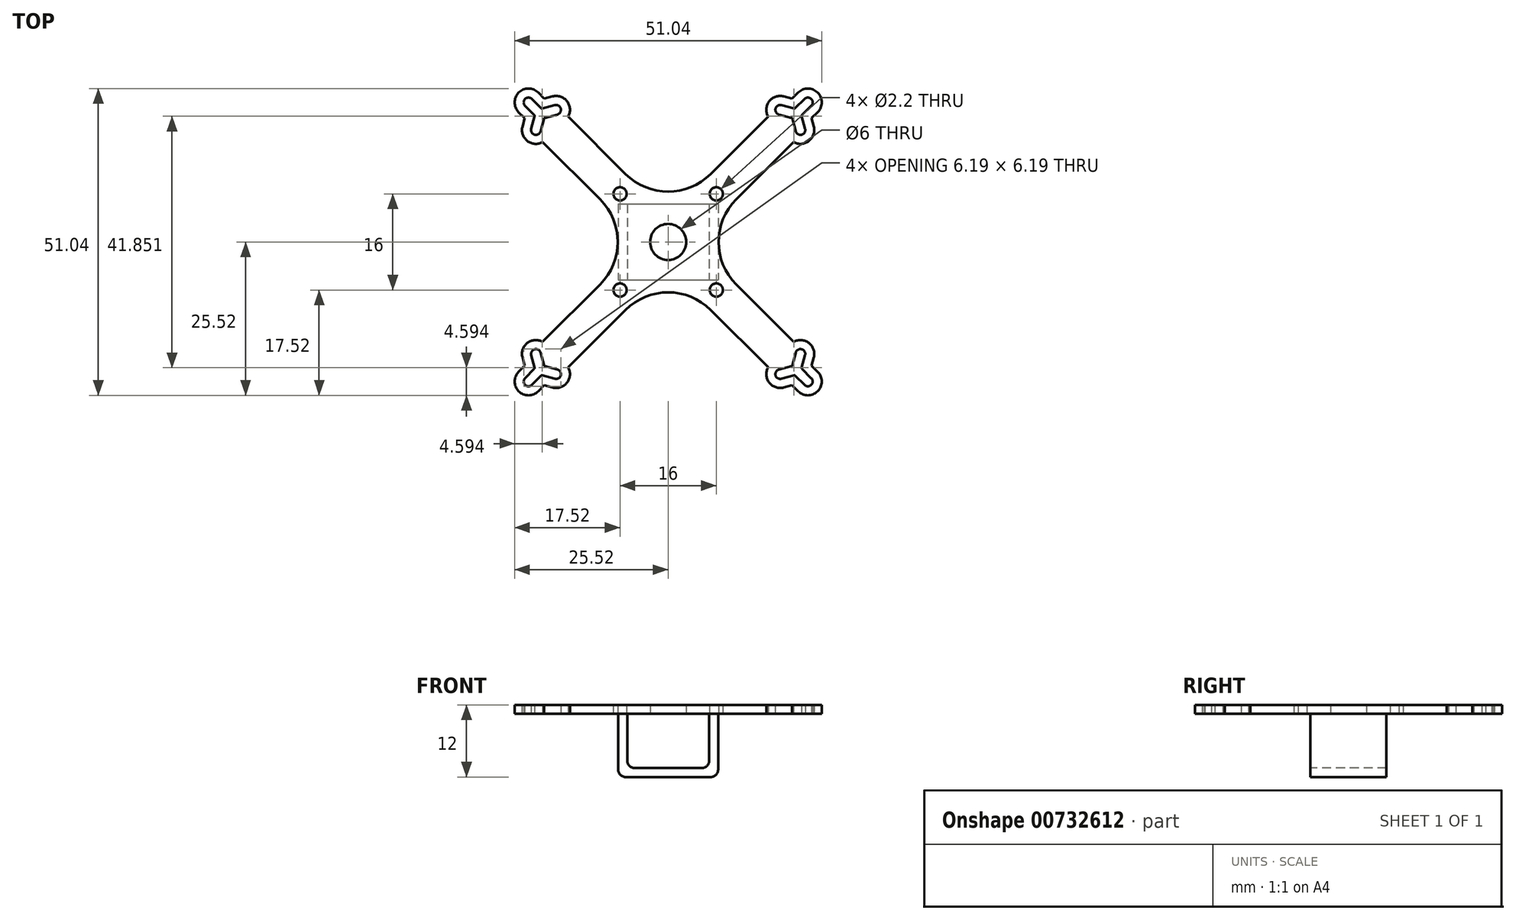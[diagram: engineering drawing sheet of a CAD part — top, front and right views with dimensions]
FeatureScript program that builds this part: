
annotation { "Feature Type Name" : "Feature", "Feature Type Description" : "" }
export const myFeature = defineFeature(function(context is Context, id is Id, definition is map)
    precondition{}
    {
        {
            var Q0;
            Q0=qCreatedBy(makeId("Top.planeOp"),FACE);
            var sketch = newSketch(context, id + "F0", { "sketchPlane" : qUnion([Q0])});
            skLineSegment(sketch, "E0", {"start": v(-7, 6.31) * mm, "end": v(7, 6.31) * mm});
            skLineSegment(sketch, "E1", {"start": v(-7, -6.31) * mm, "end": v(7, -6.31) * mm});
            skPoint(sketch, "E2.middle", {"position": v(0, 0) * mm});
            skLineSegment(sketch, "E3", {"start": v(-10, 10) * mm, "end": v(-8, 8) * mm, "construction": true});
            skPoint(sketch, "E4.center", {"position": v(-21.28, -21.28) * mm});
            skLineSegment(sketch, "E5.0", {"start": v(-20.94, -22.2) * mm, "end": v(-18.83, -22.76) * mm});
            skLineSegment(sketch, "E6.0", {"start": v(-20.53, -20.65) * mm, "end": v(-18.41, -21.22) * mm});
            skLineSegment(sketch, "E7.1.0", {"start": v(-22.24, -21.11) * mm, "end": v(-23.79, -22.66) * mm});
            skLineSegment(sketch, "E7.1.1", {"start": v(-21.11, -22.24) * mm, "end": v(-22.66, -23.79) * mm});
            skLineSegment(sketch, "E7.2.0", {"start": v(-20.65, -20.53) * mm, "end": v(-21.22, -18.41) * mm});
            skLineSegment(sketch, "E7.2.1", {"start": v(-22.2, -20.94) * mm, "end": v(-22.76, -18.83) * mm});
            skPoint(sketch, "E8.visualSharp", {"position": v(-22.17, -21.04) * mm});
            skArc(sketch, "E8.filletArc", {"start": v(-22.24, -21.11) * mm, "mid": v(-22.2, -21.03) * mm, "end": v(-22.2, -20.94) * mm});
            skPoint(sketch, "E9.visualSharp", {"position": v(-20.62, -20.62) * mm});
            skArc(sketch, "E9.filletArc", {"start": v(-20.65, -20.53) * mm, "mid": v(-20.6, -20.6) * mm, "end": v(-20.53, -20.65) * mm});
            skPoint(sketch, "E10.visualSharp", {"position": v(-21.04, -22.17) * mm});
            skArc(sketch, "E10.filletArc", {"start": v(-20.94, -22.2) * mm, "mid": v(-21.03, -22.2) * mm, "end": v(-21.11, -22.24) * mm});
            skLineSegment(sketch, "E11.0", {"start": v(-23.84, -20.6) * mm, "end": v(-24.21, -19.22) * mm});
            skLineSegment(sketch, "E12.0", {"start": v(-23.84, -20.6) * mm, "end": v(-24.85, -21.6) * mm});
            skArc(sketch, "E13.0", {"start": v(-19.53, -24.1) * mm, "mid": v(-16.91, -23.53) * mm, "end": v(-16.62, -20.86) * mm});
            skLineSegment(sketch, "E14.0", {"start": v(-20.6, -23.84) * mm, "end": v(-19.22, -24.21) * mm});
            skLineSegment(sketch, "E15.0", {"start": v(-20.6, -23.84) * mm, "end": v(-21.6, -24.85) * mm});
            skArc(sketch, "E16.0", {"start": v(-24.85, -21.6) * mm, "mid": v(-24.85, -24.85) * mm, "end": v(-21.6, -24.85) * mm});
            skArc(sketch, "E17", {"start": v(-23.79, -22.66) * mm, "mid": v(-23.79, -23.79) * mm, "end": v(-22.66, -23.79) * mm});
            skArc(sketch, "E18.1.0", {"start": v(-18.83, -22.76) * mm, "mid": v(-17.85, -22.2) * mm, "end": v(-18.41, -21.22) * mm});
            skArc(sketch, "E18.2.0", {"start": v(-21.22, -18.41) * mm, "mid": v(-22.2, -17.85) * mm, "end": v(-22.76, -18.83) * mm});
            skArc(sketch, "E19.trimOffspring", {"start": v(-20.86, -16.62) * mm, "mid": v(-23.53, -16.91) * mm, "end": v(-24.1, -19.53) * mm});
            skLineSegment(sketch, "E20.1.2", {"start": v(20.94, -22.2) * mm, "end": v(18.83, -22.76) * mm});
            skArc(sketch, "E20.1.3", {"start": v(16.62, -20.86) * mm, "mid": v(16.91, -23.53) * mm, "end": v(19.53, -24.1) * mm});
            skArc(sketch, "E20.1.4", {"start": v(18.41, -21.22) * mm, "mid": v(17.85, -22.2) * mm, "end": v(18.83, -22.76) * mm});
            skLineSegment(sketch, "E20.1.5", {"start": v(20.65, -20.53) * mm, "end": v(21.22, -18.41) * mm});
            skArc(sketch, "E20.1.6", {"start": v(21.6, -24.85) * mm, "mid": v(24.85, -24.85) * mm, "end": v(24.85, -21.6) * mm});
            skLineSegment(sketch, "E20.1.7", {"start": v(22.2, -20.94) * mm, "end": v(22.76, -18.83) * mm});
            skArc(sketch, "E20.1.8", {"start": v(22.76, -18.83) * mm, "mid": v(22.2, -17.85) * mm, "end": v(21.22, -18.41) * mm});
            skPoint(sketch, "E20.1.9", {"position": v(22.17, -21.04) * mm});
            skLineSegment(sketch, "E20.1.10", {"start": v(20.53, -20.65) * mm, "end": v(18.41, -21.22) * mm});
            skLineSegment(sketch, "E20.1.11", {"start": v(23.84, -20.6) * mm, "end": v(24.85, -21.6) * mm});
            skPoint(sketch, "E20.1.12", {"position": v(21.28, -21.28) * mm});
            skLineSegment(sketch, "E20.1.13", {"start": v(22.24, -21.11) * mm, "end": v(23.79, -22.66) * mm});
            skLineSegment(sketch, "E20.1.14", {"start": v(23.84, -20.6) * mm, "end": v(24.21, -19.22) * mm});
            skLineSegment(sketch, "E20.1.15", {"start": v(20.6, -23.84) * mm, "end": v(21.6, -24.85) * mm});
            skLineSegment(sketch, "E20.1.16", {"start": v(21.11, -22.24) * mm, "end": v(22.66, -23.79) * mm});
            skArc(sketch, "E20.1.17", {"start": v(24.1, -19.53) * mm, "mid": v(23.53, -16.91) * mm, "end": v(20.86, -16.62) * mm});
            skLineSegment(sketch, "E20.1.18", {"start": v(20.6, -23.84) * mm, "end": v(19.22, -24.21) * mm});
            skArc(sketch, "E20.1.19", {"start": v(22.66, -23.79) * mm, "mid": v(23.79, -23.79) * mm, "end": v(23.79, -22.66) * mm});
            skPoint(sketch, "E20.1.20", {"position": v(20.62, -20.62) * mm});
            skPoint(sketch, "E20.1.21", {"position": v(21.04, -22.17) * mm});
            skPoint(sketch, "E20.1.22", {"position": v(21.28, -21.28) * mm});
            skPoint(sketch, "E20.1.23", {"position": v(21.28, -21.28) * mm});
            skArc(sketch, "E20.1.24", {"start": v(22.2, -20.94) * mm, "mid": v(22.2, -21.03) * mm, "end": v(22.24, -21.11) * mm});
            skArc(sketch, "E20.1.25", {"start": v(21.11, -22.24) * mm, "mid": v(21.03, -22.2) * mm, "end": v(20.94, -22.2) * mm});
            skArc(sketch, "E20.1.26", {"start": v(20.53, -20.65) * mm, "mid": v(20.6, -20.6) * mm, "end": v(20.65, -20.53) * mm});
            skLineSegment(sketch, "E20.2.2", {"start": v(22.2, 20.94) * mm, "end": v(22.76, 18.83) * mm});
            skArc(sketch, "E20.2.3", {"start": v(20.86, 16.62) * mm, "mid": v(23.53, 16.91) * mm, "end": v(24.1, 19.53) * mm});
            skArc(sketch, "E20.2.4", {"start": v(21.22, 18.41) * mm, "mid": v(22.2, 17.85) * mm, "end": v(22.76, 18.83) * mm});
            skLineSegment(sketch, "E20.2.5", {"start": v(20.53, 20.65) * mm, "end": v(18.41, 21.22) * mm});
            skArc(sketch, "E20.2.6", {"start": v(24.85, 21.6) * mm, "mid": v(24.85, 24.85) * mm, "end": v(21.6, 24.85) * mm});
            skLineSegment(sketch, "E20.2.7", {"start": v(20.94, 22.2) * mm, "end": v(18.83, 22.76) * mm});
            skArc(sketch, "E20.2.8", {"start": v(18.83, 22.76) * mm, "mid": v(17.85, 22.2) * mm, "end": v(18.41, 21.22) * mm});
            skPoint(sketch, "E20.2.9", {"position": v(21.04, 22.17) * mm});
            skLineSegment(sketch, "E20.2.10", {"start": v(20.65, 20.53) * mm, "end": v(21.22, 18.41) * mm});
            skLineSegment(sketch, "E20.2.11", {"start": v(20.6, 23.84) * mm, "end": v(21.6, 24.85) * mm});
            skPoint(sketch, "E20.2.12", {"position": v(21.28, 21.28) * mm});
            skLineSegment(sketch, "E20.2.13", {"start": v(21.11, 22.24) * mm, "end": v(22.66, 23.79) * mm});
            skLineSegment(sketch, "E20.2.14", {"start": v(20.6, 23.84) * mm, "end": v(19.22, 24.21) * mm});
            skLineSegment(sketch, "E20.2.15", {"start": v(23.84, 20.6) * mm, "end": v(24.85, 21.6) * mm});
            skLineSegment(sketch, "E20.2.16", {"start": v(22.24, 21.11) * mm, "end": v(23.79, 22.66) * mm});
            skArc(sketch, "E20.2.17", {"start": v(19.53, 24.1) * mm, "mid": v(16.91, 23.53) * mm, "end": v(16.62, 20.86) * mm});
            skLineSegment(sketch, "E20.2.18", {"start": v(23.84, 20.6) * mm, "end": v(24.21, 19.22) * mm});
            skArc(sketch, "E20.2.19", {"start": v(23.79, 22.66) * mm, "mid": v(23.79, 23.79) * mm, "end": v(22.66, 23.79) * mm});
            skPoint(sketch, "E20.2.20", {"position": v(20.62, 20.62) * mm});
            skPoint(sketch, "E20.2.21", {"position": v(22.17, 21.04) * mm});
            skPoint(sketch, "E20.2.22", {"position": v(21.28, 21.28) * mm});
            skPoint(sketch, "E20.2.23", {"position": v(21.28, 21.28) * mm});
            skArc(sketch, "E20.2.24", {"start": v(20.94, 22.2) * mm, "mid": v(21.03, 22.2) * mm, "end": v(21.11, 22.24) * mm});
            skArc(sketch, "E20.2.25", {"start": v(22.24, 21.11) * mm, "mid": v(22.2, 21.03) * mm, "end": v(22.2, 20.94) * mm});
            skArc(sketch, "E20.2.26", {"start": v(20.65, 20.53) * mm, "mid": v(20.6, 20.6) * mm, "end": v(20.53, 20.65) * mm});
            skLineSegment(sketch, "E20.3.2", {"start": v(-20.94, 22.2) * mm, "end": v(-18.83, 22.76) * mm});
            skArc(sketch, "E20.3.3", {"start": v(-16.62, 20.86) * mm, "mid": v(-16.91, 23.53) * mm, "end": v(-19.53, 24.1) * mm});
            skArc(sketch, "E20.3.4", {"start": v(-18.41, 21.22) * mm, "mid": v(-17.85, 22.2) * mm, "end": v(-18.83, 22.76) * mm});
            skLineSegment(sketch, "E20.3.5", {"start": v(-20.65, 20.53) * mm, "end": v(-21.22, 18.41) * mm});
            skArc(sketch, "E20.3.6", {"start": v(-21.6, 24.85) * mm, "mid": v(-24.85, 24.85) * mm, "end": v(-24.85, 21.6) * mm});
            skLineSegment(sketch, "E20.3.7", {"start": v(-22.2, 20.94) * mm, "end": v(-22.76, 18.83) * mm});
            skArc(sketch, "E20.3.8", {"start": v(-22.76, 18.83) * mm, "mid": v(-22.2, 17.85) * mm, "end": v(-21.22, 18.41) * mm});
            skPoint(sketch, "E20.3.9", {"position": v(-22.17, 21.04) * mm});
            skLineSegment(sketch, "E20.3.10", {"start": v(-20.53, 20.65) * mm, "end": v(-18.41, 21.22) * mm});
            skLineSegment(sketch, "E20.3.11", {"start": v(-23.84, 20.6) * mm, "end": v(-24.85, 21.6) * mm});
            skPoint(sketch, "E20.3.12", {"position": v(-21.28, 21.28) * mm});
            skLineSegment(sketch, "E20.3.13", {"start": v(-22.24, 21.11) * mm, "end": v(-23.79, 22.66) * mm});
            skLineSegment(sketch, "E20.3.14", {"start": v(-23.84, 20.6) * mm, "end": v(-24.21, 19.22) * mm});
            skLineSegment(sketch, "E20.3.15", {"start": v(-20.6, 23.84) * mm, "end": v(-21.6, 24.85) * mm});
            skLineSegment(sketch, "E20.3.16", {"start": v(-21.11, 22.24) * mm, "end": v(-22.66, 23.79) * mm});
            skArc(sketch, "E20.3.17", {"start": v(-24.1, 19.53) * mm, "mid": v(-23.53, 16.91) * mm, "end": v(-20.86, 16.62) * mm});
            skLineSegment(sketch, "E20.3.18", {"start": v(-20.6, 23.84) * mm, "end": v(-19.22, 24.21) * mm});
            skArc(sketch, "E20.3.19", {"start": v(-22.66, 23.79) * mm, "mid": v(-23.79, 23.79) * mm, "end": v(-23.79, 22.66) * mm});
            skPoint(sketch, "E20.3.20", {"position": v(-20.62, 20.62) * mm});
            skPoint(sketch, "E20.3.21", {"position": v(-21.04, 22.17) * mm});
            skPoint(sketch, "E20.3.22", {"position": v(-21.28, 21.28) * mm});
            skPoint(sketch, "E20.3.23", {"position": v(-21.28, 21.28) * mm});
            skArc(sketch, "E20.3.24", {"start": v(-22.2, 20.94) * mm, "mid": v(-22.2, 21.03) * mm, "end": v(-22.24, 21.11) * mm});
            skArc(sketch, "E20.3.25", {"start": v(-21.11, 22.24) * mm, "mid": v(-21.03, 22.2) * mm, "end": v(-20.94, 22.2) * mm});
            skArc(sketch, "E20.3.26", {"start": v(-20.53, 20.65) * mm, "mid": v(-20.6, 20.6) * mm, "end": v(-20.65, 20.53) * mm});
            skCircle(sketch, "E21", {"center": v(0, 0) * mm, "radius": 3 * mm});
            skLineSegment(sketch, "E22", {"start": v(-20.86, -16.62) * mm, "end": v(-11.31, -7.07) * mm});
            skLineSegment(sketch, "E23", {"start": v(-16.62, -20.86) * mm, "end": v(-7.07, -11.31) * mm});
            skLineSegment(sketch, "E24", {"start": v(-20.86, 16.62) * mm, "end": v(-11.31, 7.07) * mm});
            skLineSegment(sketch, "E25", {"start": v(-16.62, 20.86) * mm, "end": v(-7.07, 11.31) * mm});
            skLineSegment(sketch, "E26.trimOffspring", {"start": v(7.07, 11.31) * mm, "end": v(16.62, 20.86) * mm});
            skLineSegment(sketch, "E27.trimOffspring", {"start": v(11.31, -7.07) * mm, "end": v(20.86, -16.62) * mm});
            skLineSegment(sketch, "E28.trimOffspring", {"start": v(7.07, -11.31) * mm, "end": v(16.62, -20.86) * mm});
            skLineSegment(sketch, "E29.trimOffspring", {"start": v(11.31, 7.07) * mm, "end": v(20.86, 16.62) * mm});
            skPoint(sketch, "E30.visualSharp", {"position": v(-4.24, 0) * mm});
            skPoint(sketch, "E31.visualSharp", {"position": v(0, 4.24) * mm});
            skPoint(sketch, "E32.visualSharp", {"position": v(0, -4.24) * mm});
            skPoint(sketch, "E33.visualSharp", {"position": v(4.24, 0) * mm});
            skLineSegment(sketch, "E34", {"start": v(0, 6.31) * mm, "end": v(0, -6.31) * mm, "construction": true});
            skArc(sketch, "E35.filletArc", {"start": v(-11.31, -7.07) * mm, "mid": v(-8.38, 0) * mm, "end": v(-11.31, 7.07) * mm});
            skArc(sketch, "E36.filletArc", {"start": v(-7.07, 11.31) * mm, "mid": v(0, 8.38) * mm, "end": v(7.07, 11.31) * mm});
            skArc(sketch, "E37.filletArc", {"start": v(11.31, 7.07) * mm, "mid": v(8.38, 0) * mm, "end": v(11.31, -7.07) * mm});
            skArc(sketch, "E38.filletArc", {"start": v(7.07, -11.31) * mm, "mid": v(0, -8.38) * mm, "end": v(-7.07, -11.31) * mm});
            skLineSegment(sketch, "E39.0", {"start": v(-8.3, 6.31) * mm, "end": v(-8.3, -6.31) * mm});
            skLineSegment(sketch, "E40.0", {"start": v(8.3, 6.31) * mm, "end": v(8.3, -6.31) * mm});
            skLineSegment(sketch, "E41", {"start": v(-8.3, 6.31) * mm, "end": v(8.3, 6.31) * mm});
            skLineSegment(sketch, "E42", {"start": v(-8.3, -6.31) * mm, "end": v(8.3, -6.31) * mm});
            skPoint(sketch, "E43", {"position": v(-25.82, 23.88) * mm});
            skLineSegment(sketch, "E44", {"start": v(-25.26, 25.26) * mm, "end": v(-23.22, 23.22) * mm, "construction": true});
            skPoint(sketch, "E45.MirrorP", {"position": v(-23.88, 25.82) * mm});
            skLineSegment(sketch, "E46", {"start": v(-21.28, 21.28) * mm, "end": v(21.28, -21.28) * mm, "construction": true});
            skCircle(sketch, "E47", {"center": v(-8, 8) * mm, "radius": 1.1 * mm});
            skCircle(sketch, "E48.MirrorC", {"center": v(8, 8) * mm, "radius": 1.1 * mm});
            skCircle(sketch, "E49.MirrorC", {"center": v(-8, -8) * mm, "radius": 1.1 * mm});
            skCircle(sketch, "E50.MirrorC", {"center": v(8, -8) * mm, "radius": 1.1 * mm});
            skLineSegment(sketch, "E51", {"start": v(-25.51, 22.99) * mm, "end": v(-22.99, 25.51) * mm, "construction": true});
            skSolve(sketch);
        }
        {
            var Q0;
            Q0=makeQuery(id+"F0.imprint","IMPRINT",FACE,{"disambiguationData":[TD([[makeQuery(id+"F0.imprint","IMPRINT",EDGE,{"derivedFrom":sQuery(id+"F0.wireOp",EDGE,"E21")}),-1.0]])]});
            var Q1;
            Q1=makeQuery(id+"F0.imprint","IMPRINT",FACE,{"disambiguationData":[TD([[makeQuery(id+"F0.imprint","IMPRINT",EDGE,{"derivedFrom":sQuery(id+"F0.wireOp",EDGE,"E21")}),1.0]])]});
            extrude(context, id + "F1", {"entities" : qUnion([Q0, Q1]), "oppositeDirection" : true, "depth" : 10.5 * mm, "offsetDistance" : 25 * mm});
        }
        {
            var Q0;
            Q0=makeQuery(id+"F0.imprint","IMPRINT",FACE,{"disambiguationData":[TD([[makeQuery(id+"F0.imprint","IMPRINT",EDGE,{"derivedFrom":sQuery(id+"F0.wireOp",EDGE,"E5.0")}),-1.0]])]});
            var sketch = newSketch(context, id + "F2", { "sketchPlane" : qUnion([Q0])});
            skSolve(sketch);
        }
        {
            var Q0;
            Q0=makeQuery(id+"F2.imprint","IMPRINT",FACE,{"disambiguationData":[TD([[makeQuery(id+"F2.imprint","IMPRINT",EDGE,{"derivedFrom":makeQuery(id+"F0.imprint","IMPRINT",EDGE,{"derivedFrom":sQuery(id+"F0.wireOp",EDGE,"E5.0")})}),-1.0]])]});
            var Q1;
            Q1=makeQuery(id+"F0.imprint","IMPRINT",FACE,{"disambiguationData":[TD([[makeQuery(id+"F0.imprint","IMPRINT",EDGE,{"derivedFrom":sQuery(id+"F0.wireOp",EDGE,"E21")}),-1.0]])]});
            extrude(context, id + "F3", {"entities" : qUnion([Q0, Q1]), "operationType" : NewBodyOperationType.ADD, "depth" : 1.5 * mm, "offsetDistance" : 25 * mm});
        }
        {
            var Q0;
            Q0=makeQuery(id+"F1.opExtrude","SWEPT_FACE",FACE,{"disambiguationData":[OSD([sQuery(id+"F0.wireOp",EDGE,"E42")])]});
            var sketch = newSketch(context, id + "F4", { "sketchPlane" : qUnion([Q0])});
            skLineSegment(sketch, "E52.0", {"start": v(-6.8, -9) * mm, "end": v(6.8, -9) * mm});
            skLineSegment(sketch, "E53.0", {"start": v(-6.8, -9) * mm, "end": v(-6.8, 0) * mm});
            skLineSegment(sketch, "E54.0", {"start": v(6.8, -9) * mm, "end": v(6.8, 0) * mm});
            skSolve(sketch);
        }
        {
            var Q0;
            Q0=makeQuery(id+"F4.imprint","IMPRINT",FACE,{"disambiguationData":[TD([[makeQuery(id+"F4.imprint","IMPRINT",EDGE,{"derivedFrom":sQuery(id+"F4.wireOp",EDGE,"E52.0")}),1.0]])]});
            extrude(context, id + "F5", {"entities" : qUnion([Q0]), "operationType" : NewBodyOperationType.REMOVE, "oppositeDirection" : true, "depth" : 25 * mm, "offsetDistance" : 25 * mm});
        }
        {
            var Q0;
            Q0=makeQuery(id+"F1.opExtrude","CAP_EDGE",EDGE,{"disambiguationData":[OSD([sQuery(id+"F0.wireOp",EDGE,"E40.0")])],"isStart":false});
            var Q1;
            Q1=makeQuery(id+"F1.opExtrude","CAP_EDGE",EDGE,{"disambiguationData":[OSD([sQuery(id+"F0.wireOp",EDGE,"E39.0")])],"isStart":false});
            var Q2;
            Q2=makeQuery(id+"F5.boolean.opBoolean","COPY",EDGE,{"derivedFrom":makeQuery(id+"F5.opExtrude","SWEPT_EDGE",EDGE,{"disambiguationData":[OSD([sQuery(id+"F4.wireOp",EDGE,"E52.0"),sQuery(id+"F4.wireOp",EDGE,"E53.0")])]})});
            var Q3;
            Q3=makeQuery(id+"F5.boolean.opBoolean","COPY",EDGE,{"derivedFrom":makeQuery(id+"F5.opExtrude","SWEPT_EDGE",EDGE,{"disambiguationData":[OSD([sQuery(id+"F4.wireOp",EDGE,"E52.0"),sQuery(id+"F4.wireOp",EDGE,"E54.0")])]})});
            fillet(context, id + "F6", {"entities" : qUnion([Q0, Q1, Q2, Q3]), "radius" : 1.2 * mm, "tangentPropagation" : true, "allowEdgeOverflow" : false});
        }
        {
            var Q0;
            Q0=sQuery(id+"F0.wireOp",EDGE,"E51");
            cPlane(context, id + "F7", {"entities" : qUnion([Q0]), "cplaneType" : CPlaneType.LINE_ANGLE, "offset" : 25 * mm, "angle" : 90 * degree, "width" : 150 * mm, "height" : 150 * mm});
        }
    });
